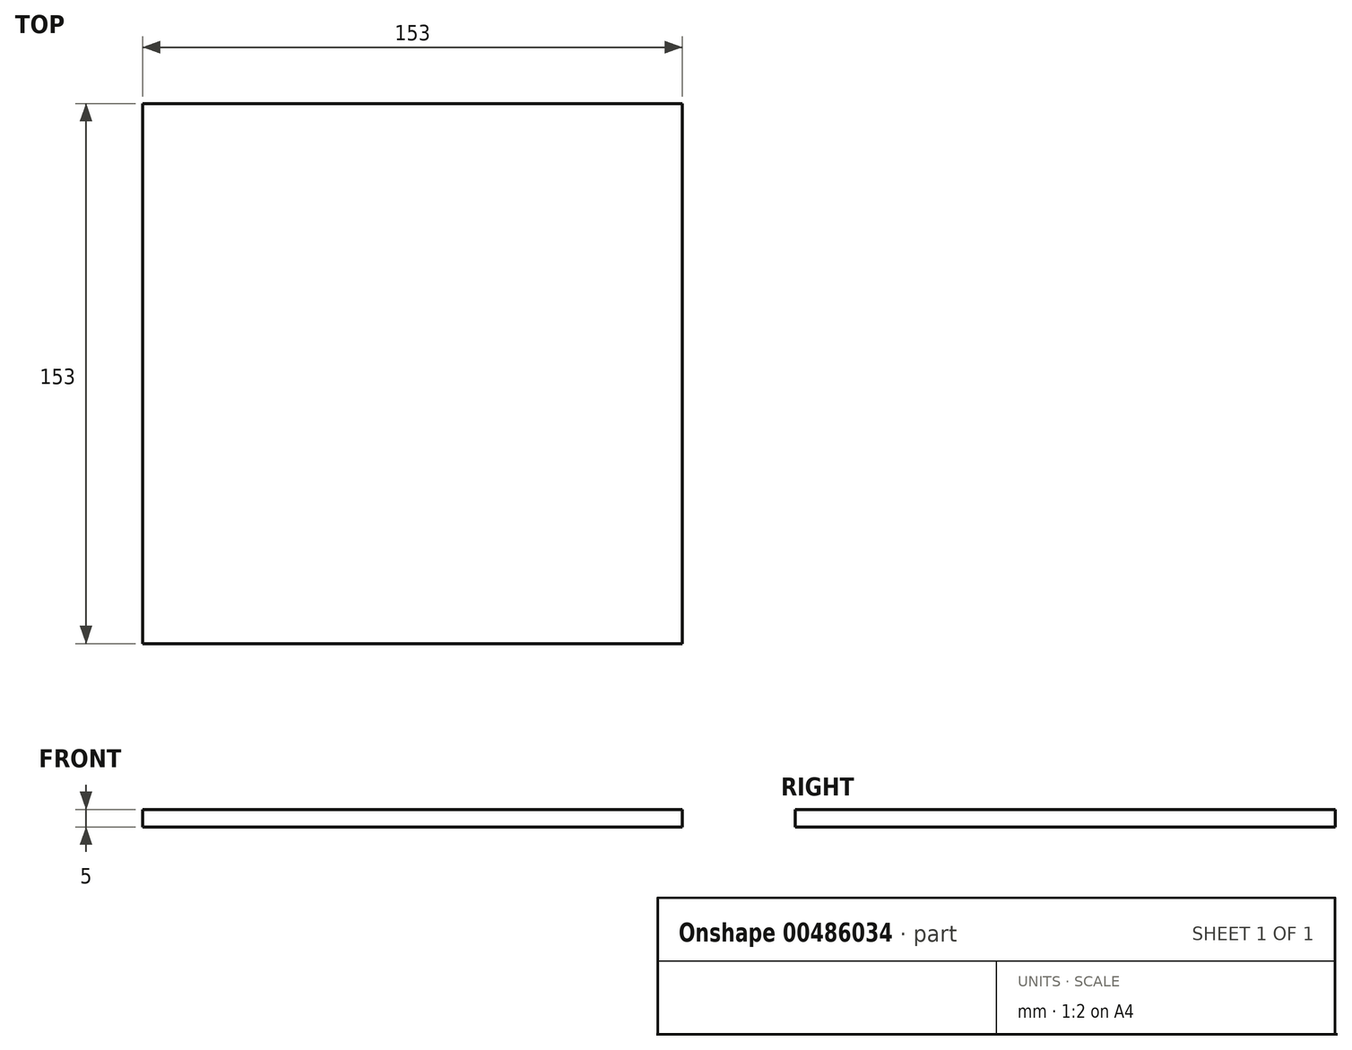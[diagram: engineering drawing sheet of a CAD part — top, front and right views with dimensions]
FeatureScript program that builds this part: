
annotation { "Feature Type Name" : "Feature", "Feature Type Description" : "" }
export const myFeature = defineFeature(function(context is Context, id is Id, definition is map)
    precondition{}
    {
        {
            var Q0;
            Q0=qCreatedBy(makeId("Top.planeOp"),FACE);
            var sketch = newSketch(context, id + "F0", { "sketchPlane" : qUnion([Q0])});
            skLineSegment(sketch, "E0.bottom", {"start": v(76.5, 76.5) * mm, "end": v(-76.5, 76.5) * mm});
            skLineSegment(sketch, "E0.top", {"start": v(76.5, -76.5) * mm, "end": v(-76.5, -76.5) * mm});
            skLineSegment(sketch, "E0.left", {"start": v(76.5, 76.5) * mm, "end": v(76.5, -76.5) * mm});
            skLineSegment(sketch, "E0.right", {"start": v(-76.5, 76.5) * mm, "end": v(-76.5, -76.5) * mm});
            skPoint(sketch, "E0.middle", {"position": v(0, 0) * mm});
            skSolve(sketch);
        }
        {
            var Q0;
            Q0=makeQuery(id+"F0.imprint","IMPRINT",FACE,{"disambiguationData":[TD([[makeQuery(id+"F0.imprint","IMPRINT",EDGE,{"derivedFrom":sQuery(id+"F0.wireOp",EDGE,"E0.bottom")}),1.0]])]});
            extrude(context, id + "F1", {"entities" : qUnion([Q0]), "depth" : 5 * mm});
        }
    });
